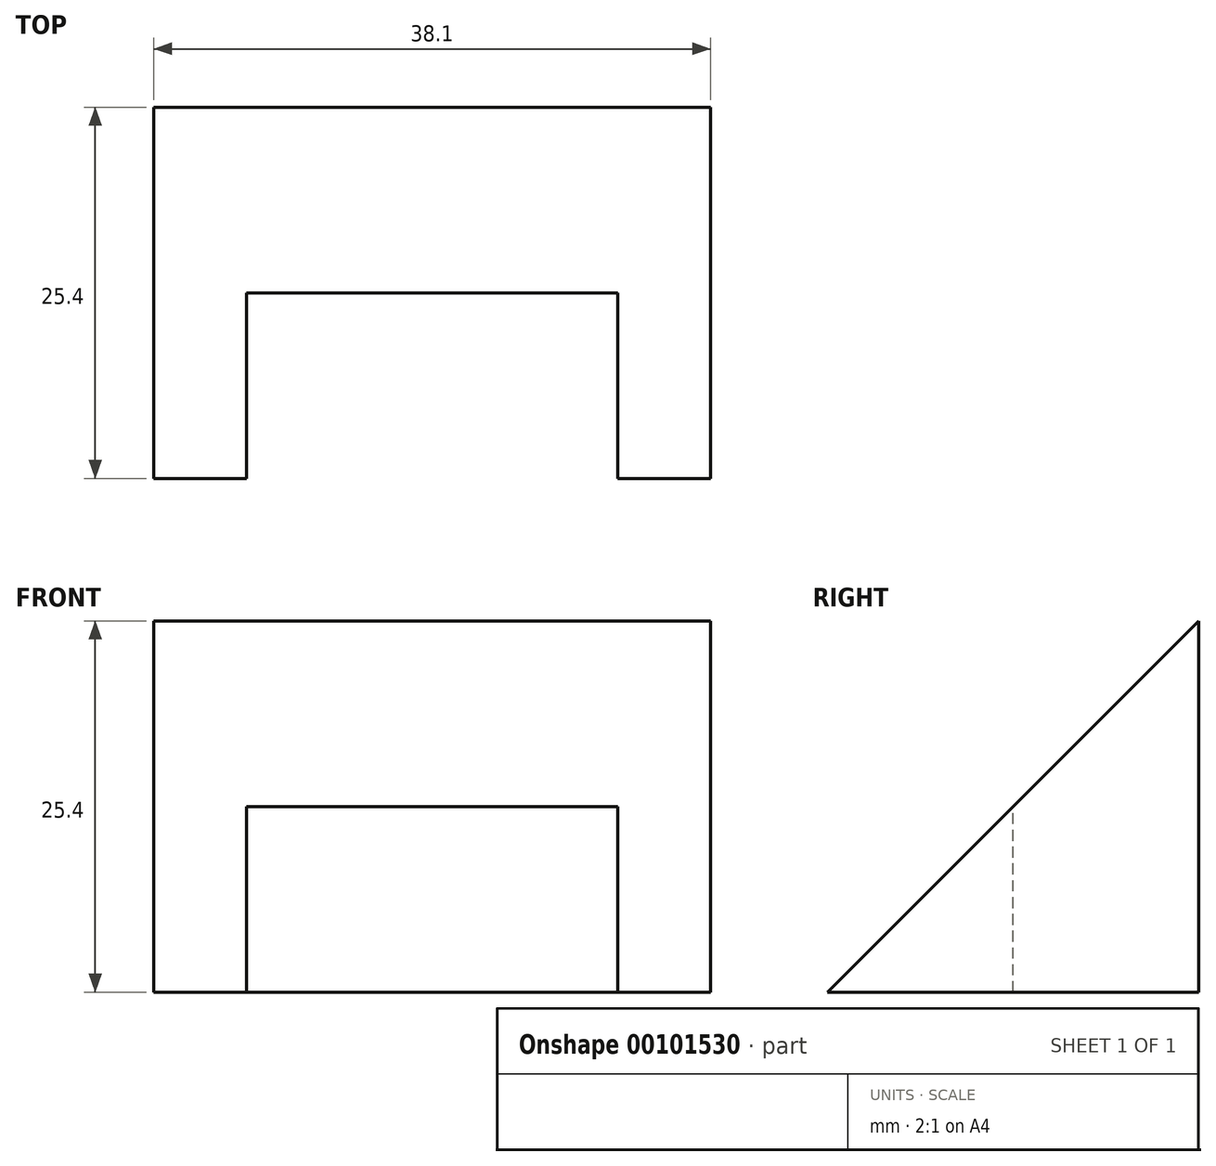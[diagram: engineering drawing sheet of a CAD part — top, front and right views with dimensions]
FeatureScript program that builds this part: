
annotation { "Feature Type Name" : "Feature", "Feature Type Description" : "" }
export const myFeature = defineFeature(function(context is Context, id is Id, definition is map)
    precondition{}
    {
        {
            var Q0;
            Q0=qCreatedBy(makeId("Right.planeOp"),FACE);
            var sketch = newSketch(context, id + "F0", { "sketchPlane" : qUnion([Q0])});
            skLineSegment(sketch, "E0", {"start": v(0, 0) * mm, "end": v(25.4, 0) * mm});
            skLineSegment(sketch, "E1", {"start": v(25.4, 0) * mm, "end": v(25.4, 25.4) * mm});
            skLineSegment(sketch, "E2", {"start": v(25.4, 25.4) * mm, "end": v(0, 0) * mm});
            skSolve(sketch);
        }
        {
            var Q0;
            Q0=makeQuery(id+"F0.imprint","IMPRINT",FACE,{"disambiguationData":[TD([[makeQuery(id+"F0.imprint","IMPRINT",EDGE,{"derivedFrom":sQuery(id+"F0.wireOp",EDGE,"E0")}),1.0]])]});
            extrude(context, id + "F1", {"entities" : qUnion([Q0]), "depth" : 38.1 * mm});
        }
        {
            var Q0;
            Q0=makeQuery(id+"F1.opExtrude","CAP_FACE",FACE,{"disambiguationData":[OSD([sQuery(id+"F0.wireOp",EDGE,"E0"),sQuery(id+"F0.wireOp",EDGE,"E1"),sQuery(id+"F0.wireOp",EDGE,"E2")])],"isStart":false});
            var sketch = newSketch(context, id + "F2", { "sketchPlane" : qUnion([Q0])});
            skLineSegment(sketch, "E3", {"start": v(0, 0) * mm, "end": v(12.7, 0) * mm});
            skLineSegment(sketch, "E4", {"start": v(12.7, 0) * mm, "end": v(12.7, 12.7) * mm});
            skLineSegment(sketch, "E5", {"start": v(12.7, 12.7) * mm, "end": v(0, 0) * mm});
            skSolve(sketch);
        }
        {
            var Q0;
            Q0 = qSketchRegion(id + "F2", true);
            extrude(context, id + "F3", {"entities" : qUnion([Q0]), "operationType" : NewBodyOperationType.REMOVE, "oppositeDirection" : true, "depth" : 31.75 * mm, "hasSecondDirection" : true, "secondDirectionOppositeDirection" : true, "secondDirectionDepth" : 6.35 * mm});
        }
    });
